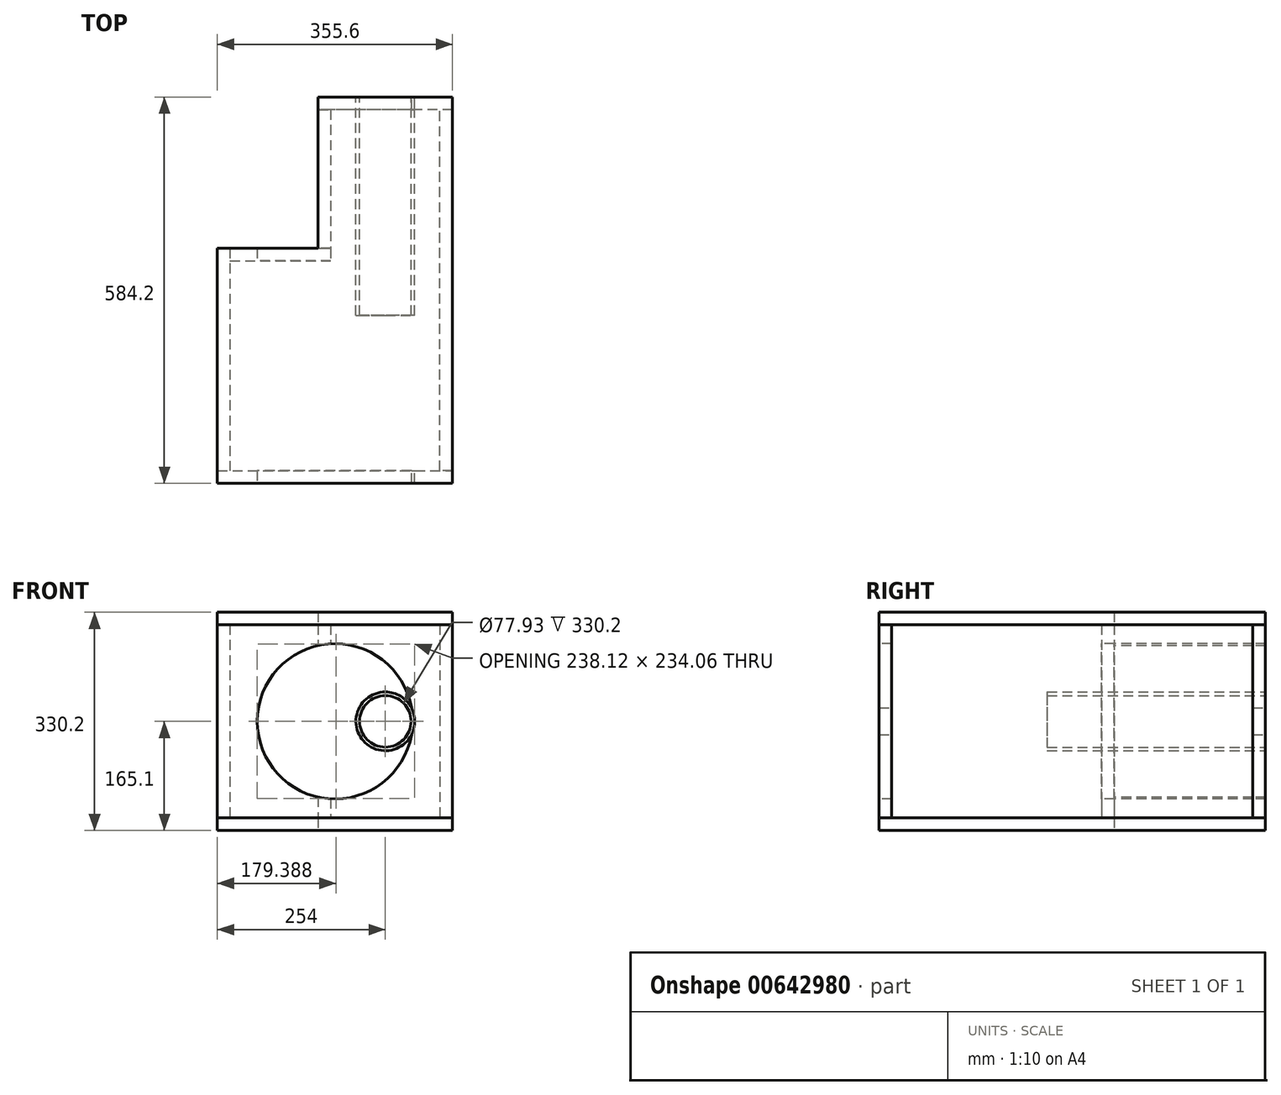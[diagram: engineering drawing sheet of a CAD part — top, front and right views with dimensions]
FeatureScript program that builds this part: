
annotation { "Feature Type Name" : "Feature", "Feature Type Description" : "" }
export const myFeature = defineFeature(function(context is Context, id is Id, definition is map)
    precondition{}
    {
        {
            var Q0;
            Q0=qCreatedBy(makeId("Top.planeOp"),FACE);
            var sketch = newSketch(context, id + "F0", { "sketchPlane" : qUnion([Q0])});
            skLineSegment(sketch, "E0.bottom", {"start": v(0, 0) * mm, "end": v(-355.6, 0) * mm});
            skLineSegment(sketch, "E0.top", {"start": v(0, 584.2) * mm, "end": v(-203.2, 584.2) * mm});
            skLineSegment(sketch, "E0.left", {"start": v(0, 0) * mm, "end": v(0, 584.2) * mm});
            skLineSegment(sketch, "E0.right", {"start": v(-355.6, 0) * mm, "end": v(-355.6, 355.6) * mm});
            skLineSegment(sketch, "E1", {"start": v(-355.6, 355.6) * mm, "end": v(-203.2, 355.6) * mm});
            skLineSegment(sketch, "E2", {"start": v(-203.2, 355.6) * mm, "end": v(-203.2, 584.2) * mm});
            skSolve(sketch);
        }
        {
            var Q0;
            Q0 = qSketchRegion(id + "F0", true);
            extrude(context, id + "F1", {"entities" : qUnion([Q0]), "depth" : 19.05 * mm, "offsetDistance" : 25.4 * mm});
        }
        {
            var Q0;
            Q0=makeQuery(id+"F1.opExtrude","CAP_FACE",FACE,{"disambiguationData":[OSD([sQuery(id+"F0.wireOp",EDGE,"E0.bottom"),sQuery(id+"F0.wireOp",EDGE,"E0.top"),sQuery(id+"F0.wireOp",EDGE,"E0.left"),sQuery(id+"F0.wireOp",EDGE,"E0.right")])],"isStart":false});
            var sketch = newSketch(context, id + "F2", { "sketchPlane" : qUnion([Q0])});
            skLineSegment(sketch, "E3.bottom", {"start": v(-355.6, 0) * mm, "end": v(0, 0) * mm});
            skLineSegment(sketch, "E3.top", {"start": v(-355.6, 19.05) * mm, "end": v(0, 19.05) * mm});
            skLineSegment(sketch, "E3.left", {"start": v(-355.6, 0) * mm, "end": v(-355.6, 19.05) * mm});
            skLineSegment(sketch, "E3.right", {"start": v(0, 0) * mm, "end": v(0, 19.05) * mm});
            skSolve(sketch);
        }
        {
            var Q0;
            Q0 = qSketchRegion(id + "F2", true);
            extrude(context, id + "F3", {"entities" : qUnion([Q0]), "depth" : 292.1 * mm, "offsetDistance" : 25.4 * mm});
        }
        {
            var Q0;
            Q0=makeQuery(id+"F1.opExtrude","CAP_FACE",FACE,{"disambiguationData":[OSD([sQuery(id+"F0.wireOp",EDGE,"E0.bottom"),sQuery(id+"F0.wireOp",EDGE,"E0.top"),sQuery(id+"F0.wireOp",EDGE,"E0.left"),sQuery(id+"F0.wireOp",EDGE,"E0.right")])],"isStart":false});
            var sketch = newSketch(context, id + "F4", { "sketchPlane" : qUnion([Q0])});
            skLineSegment(sketch, "E4.bottom", {"start": v(0, 584.2) * mm, "end": v(-203.2, 584.2) * mm});
            skLineSegment(sketch, "E4.top", {"start": v(0, 565.15) * mm, "end": v(-203.2, 565.15) * mm});
            skLineSegment(sketch, "E4.left", {"start": v(0, 584.2) * mm, "end": v(0, 565.15) * mm});
            skLineSegment(sketch, "E4.right", {"start": v(-203.2, 584.2) * mm, "end": v(-203.2, 565.15) * mm});
            skSolve(sketch);
        }
        {
            var Q0;
            Q0 = qSketchRegion(id + "F4", true);
            var Q1;
            Q1=makeQuery(id+"F3.opExtrude","CAP_FACE",FACE,{"disambiguationData":[OSD([sQuery(id+"F2.wireOp",EDGE,"E3.bottom"),sQuery(id+"F2.wireOp",EDGE,"E3.top"),sQuery(id+"F2.wireOp",EDGE,"E3.left"),sQuery(id+"F2.wireOp",EDGE,"E3.right")])],"isStart":false});
            extrude(context, id + "F5", {"entities" : qUnion([Q0]), "endBound" : BoundingType.UP_TO_SURFACE, "depth" : 25.4 * mm, "endBoundEntityFace" : qUnion([Q1]), "offsetDistance" : 25.4 * mm});
        }
        {
            var Q0;
            Q0=makeQuery(id+"F1.opExtrude","CAP_FACE",FACE,{"disambiguationData":[OSD([sQuery(id+"F0.wireOp",EDGE,"E0.bottom"),sQuery(id+"F0.wireOp",EDGE,"E0.top"),sQuery(id+"F0.wireOp",EDGE,"E0.left"),sQuery(id+"F0.wireOp",EDGE,"E0.right")])],"isStart":false});
            var sketch = newSketch(context, id + "F6", { "sketchPlane" : qUnion([Q0])});
            skLineSegment(sketch, "E5.bottom", {"start": v(0, 19.05) * mm, "end": v(-19.05, 19.05) * mm});
            skLineSegment(sketch, "E5.top", {"start": v(0, 565.15) * mm, "end": v(-19.05, 565.15) * mm});
            skLineSegment(sketch, "E5.left", {"start": v(0, 19.05) * mm, "end": v(0, 565.15) * mm});
            skLineSegment(sketch, "E5.right", {"start": v(-19.05, 19.05) * mm, "end": v(-19.05, 565.15) * mm});
            skSolve(sketch);
        }
        {
            var Q0;
            Q0 = qSketchRegion(id + "F6", true);
            var Q1;
            Q1=makeQuery(id+"F3.opExtrude","CAP_FACE",FACE,{"disambiguationData":[OSD([sQuery(id+"F2.wireOp",EDGE,"E3.bottom"),sQuery(id+"F2.wireOp",EDGE,"E3.top"),sQuery(id+"F2.wireOp",EDGE,"E3.left"),sQuery(id+"F2.wireOp",EDGE,"E3.right")])],"isStart":false});
            extrude(context, id + "F7", {"entities" : qUnion([Q0]), "endBound" : BoundingType.UP_TO_SURFACE, "depth" : 25.4 * mm, "endBoundEntityFace" : qUnion([Q1]), "offsetDistance" : 25.4 * mm});
        }
        {
            var Q0;
            Q0=makeQuery(id+"F1.opExtrude","CAP_FACE",FACE,{"disambiguationData":[OSD([sQuery(id+"F0.wireOp",EDGE,"E0.bottom"),sQuery(id+"F0.wireOp",EDGE,"E0.top"),sQuery(id+"F0.wireOp",EDGE,"E0.left"),sQuery(id+"F0.wireOp",EDGE,"E0.right"),sQuery(id+"F0.wireOp",EDGE,"E1"),sQuery(id+"F0.wireOp",EDGE,"E2")])],"isStart":false});
            var sketch = newSketch(context, id + "F8", { "sketchPlane" : qUnion([Q0])});
            skLineSegment(sketch, "E6.bottom", {"start": v(-355.6, 355.6) * mm, "end": v(-336.55, 355.6) * mm});
            skLineSegment(sketch, "E6.top", {"start": v(-355.6, 19.05) * mm, "end": v(-336.55, 19.05) * mm});
            skLineSegment(sketch, "E6.left", {"start": v(-355.6, 355.6) * mm, "end": v(-355.6, 19.05) * mm});
            skLineSegment(sketch, "E6.right", {"start": v(-336.55, 355.6) * mm, "end": v(-336.55, 19.05) * mm});
            skSolve(sketch);
        }
        {
            var Q0;
            Q0 = qSketchRegion(id + "F8", true);
            var Q1;
            Q1=makeQuery(id+"F3.opExtrude","CAP_FACE",FACE,{"disambiguationData":[OSD([sQuery(id+"F2.wireOp",EDGE,"E3.bottom"),sQuery(id+"F2.wireOp",EDGE,"E3.top"),sQuery(id+"F2.wireOp",EDGE,"E3.left"),sQuery(id+"F2.wireOp",EDGE,"E3.right")])],"isStart":false});
            extrude(context, id + "F9", {"entities" : qUnion([Q0]), "endBound" : BoundingType.UP_TO_SURFACE, "depth" : 25.4 * mm, "endBoundEntityFace" : qUnion([Q1]), "offsetDistance" : 25.4 * mm});
        }
        {
            var Q0;
            Q0=makeQuery(id+"F1.opExtrude","CAP_FACE",FACE,{"disambiguationData":[OSD([sQuery(id+"F0.wireOp",EDGE,"E0.bottom"),sQuery(id+"F0.wireOp",EDGE,"E0.top"),sQuery(id+"F0.wireOp",EDGE,"E0.left"),sQuery(id+"F0.wireOp",EDGE,"E0.right"),sQuery(id+"F0.wireOp",EDGE,"E1"),sQuery(id+"F0.wireOp",EDGE,"E2")])],"isStart":false});
            var sketch = newSketch(context, id + "F10", { "sketchPlane" : qUnion([Q0])});
            skLineSegment(sketch, "E7.bottom", {"start": v(-203.2, 355.6) * mm, "end": v(-184.15, 355.6) * mm});
            skLineSegment(sketch, "E7.top", {"start": v(-203.2, 565.15) * mm, "end": v(-184.15, 565.15) * mm});
            skLineSegment(sketch, "E7.left", {"start": v(-203.2, 355.6) * mm, "end": v(-203.2, 565.15) * mm});
            skLineSegment(sketch, "E7.right", {"start": v(-184.15, 355.6) * mm, "end": v(-184.15, 565.15) * mm});
            skSolve(sketch);
        }
        {
            var Q0;
            Q0 = qSketchRegion(id + "F10", true);
            var Q1;
            Q1=makeQuery(id+"F3.opExtrude","CAP_FACE",FACE,{"disambiguationData":[OSD([sQuery(id+"F2.wireOp",EDGE,"E3.bottom"),sQuery(id+"F2.wireOp",EDGE,"E3.top"),sQuery(id+"F2.wireOp",EDGE,"E3.left"),sQuery(id+"F2.wireOp",EDGE,"E3.right")])],"isStart":false});
            extrude(context, id + "F11", {"entities" : qUnion([Q0]), "endBound" : BoundingType.UP_TO_SURFACE, "depth" : 25.4 * mm, "endBoundEntityFace" : qUnion([Q1]), "offsetDistance" : 25.4 * mm});
        }
        {
            var Q0;
            Q0=makeQuery(id+"F1.opExtrude","CAP_FACE",FACE,{"disambiguationData":[OSD([sQuery(id+"F0.wireOp",EDGE,"E0.bottom"),sQuery(id+"F0.wireOp",EDGE,"E0.top"),sQuery(id+"F0.wireOp",EDGE,"E0.left"),sQuery(id+"F0.wireOp",EDGE,"E0.right"),sQuery(id+"F0.wireOp",EDGE,"E1"),sQuery(id+"F0.wireOp",EDGE,"E2")])],"isStart":false});
            var sketch = newSketch(context, id + "F12", { "sketchPlane" : qUnion([Q0])});
            skLineSegment(sketch, "E8.bottom", {"start": v(-336.55, 355.6) * mm, "end": v(-184.15, 355.6) * mm});
            skLineSegment(sketch, "E8.top", {"start": v(-336.55, 336.55) * mm, "end": v(-184.15, 336.55) * mm});
            skLineSegment(sketch, "E8.left", {"start": v(-336.55, 355.6) * mm, "end": v(-336.55, 336.55) * mm});
            skLineSegment(sketch, "E8.right", {"start": v(-184.15, 355.6) * mm, "end": v(-184.15, 336.55) * mm});
            skSolve(sketch);
        }
        {
            var Q0;
            Q0 = qSketchRegion(id + "F12", true);
            var Q1;
            Q1=makeQuery(id+"F3.opExtrude","CAP_FACE",FACE,{"disambiguationData":[OSD([sQuery(id+"F2.wireOp",EDGE,"E3.bottom"),sQuery(id+"F2.wireOp",EDGE,"E3.top"),sQuery(id+"F2.wireOp",EDGE,"E3.left"),sQuery(id+"F2.wireOp",EDGE,"E3.right")])],"isStart":false});
            extrude(context, id + "F13", {"entities" : qUnion([Q0]), "endBound" : BoundingType.UP_TO_SURFACE, "depth" : 25.4 * mm, "endBoundEntityFace" : qUnion([Q1]), "offsetDistance" : 25.4 * mm});
        }
        {
            var Q0;
            Q0=makeQuery(id+"F3.opExtrude","CAP_FACE",FACE,{"disambiguationData":[OSD([sQuery(id+"F2.wireOp",EDGE,"E3.bottom"),sQuery(id+"F2.wireOp",EDGE,"E3.top"),sQuery(id+"F2.wireOp",EDGE,"E3.left"),sQuery(id+"F2.wireOp",EDGE,"E3.right")])],"isStart":false});
            var sketch = newSketch(context, id + "F14", { "sketchPlane" : qUnion([Q0])});
            skLineSegment(sketch, "E9.0.0", {"start": v(0, 584.2) * mm, "end": v(0, 0) * mm});
            skLineSegment(sketch, "E9.0.1", {"start": v(0, 0) * mm, "end": v(-355.6, 0) * mm});
            skLineSegment(sketch, "E9.0.2", {"start": v(-355.6, 0) * mm, "end": v(-355.6, 355.6) * mm});
            skLineSegment(sketch, "E9.0.3", {"start": v(-355.6, 355.6) * mm, "end": v(-203.2, 355.6) * mm});
            skLineSegment(sketch, "E9.0.4", {"start": v(-203.2, 355.6) * mm, "end": v(-203.2, 584.2) * mm});
            skLineSegment(sketch, "E9.0.5", {"start": v(-203.2, 584.2) * mm, "end": v(0, 584.2) * mm});
            skSolve(sketch);
        }
        {
            var Q0;
            Q0 = qSketchRegion(id + "F14", true);
            extrude(context, id + "F15", {"entities" : qUnion([Q0]), "depth" : 19.05 * mm, "offsetDistance" : 25.4 * mm});
        }
        {
            var Q0;
            Q0=makeQuery(id+"F3.opExtrude","SWEPT_FACE",FACE,{"disambiguationData":[OSD([sQuery(id+"F2.wireOp",EDGE,"E3.bottom")])]});
            var sketch = newSketch(context, id + "F16", { "sketchPlane" : qUnion([Q0])});
            skCircle(sketch, "E10", {"center": v(-177.8, 165.1) * mm, "radius": 117.48 * mm});
            skLineSegment(sketch, "E11", {"start": v(-355.6, 165.1) * mm, "end": v(0, 165.1) * mm, "construction": true});
            skSolve(sketch);
        }
        {
            var Q0;
            Q0 = qSketchRegion(id + "F16", true);
            var Q1;
            Q1=makeQuery(id+"F3.opExtrude","SWEPT_FACE",FACE,{"disambiguationData":[OSD([sQuery(id+"F2.wireOp",EDGE,"E3.top")])]});
            extrude(context, id + "F17", {"entities" : qUnion([Q0]), "operationType" : NewBodyOperationType.REMOVE, "endBound" : BoundingType.THROUGH_ALL, "oppositeDirection" : true, "depth" : 25.4 * mm, "endBoundEntityFace" : qUnion([Q1]), "offsetDistance" : 25.4 * mm});
        }
        {
            var Q0;
            Q0=makeQuery(id+"F5.opExtrude","SWEPT_FACE",FACE,{"disambiguationData":[OSD([sQuery(id+"F4.wireOp",EDGE,"E4.bottom")])]});
            var sketch = newSketch(context, id + "F18", { "sketchPlane" : qUnion([Q0])});
            skCircle(sketch, "E12", {"center": v(101.6, 165.1) * mm, "radius": 44.45 * mm});
            skLineSegment(sketch, "E13", {"start": v(0, 165.1) * mm, "end": v(203.2, 165.1) * mm, "construction": true});
            skSolve(sketch);
        }
        {
            var Q0;
            Q0 = qSketchRegion(id + "F18", true);
            extrude(context, id + "F19", {"entities" : qUnion([Q0]), "operationType" : NewBodyOperationType.REMOVE, "endBound" : BoundingType.THROUGH_ALL, "oppositeDirection" : true, "depth" : 25.4 * mm, "offsetDistance" : 25.4 * mm});
        }
        {
            var Q0;
            Q0=makeQuery(id+"F5.opExtrude","SWEPT_FACE",FACE,{"disambiguationData":[OSD([sQuery(id+"F4.wireOp",EDGE,"E4.bottom")])]});
            var sketch = newSketch(context, id + "F20", { "sketchPlane" : qUnion([Q0])});
            skCircle(sketch, "E14", {"center": v(101.6, 165.1) * mm, "radius": 44.45 * mm});
            skCircle(sketch, "E15", {"center": v(101.6, 165.1) * mm, "radius": 38.96 * mm});
            skSolve(sketch);
        }
        {
            var Q0;
            Q0 = qSketchRegion(id + "F20", true);
            extrude(context, id + "F21", {"entities" : qUnion([Q0]), "oppositeDirection" : true, "depth" : 330.2 * mm, "offsetDistance" : 25.4 * mm});
        }
    });
